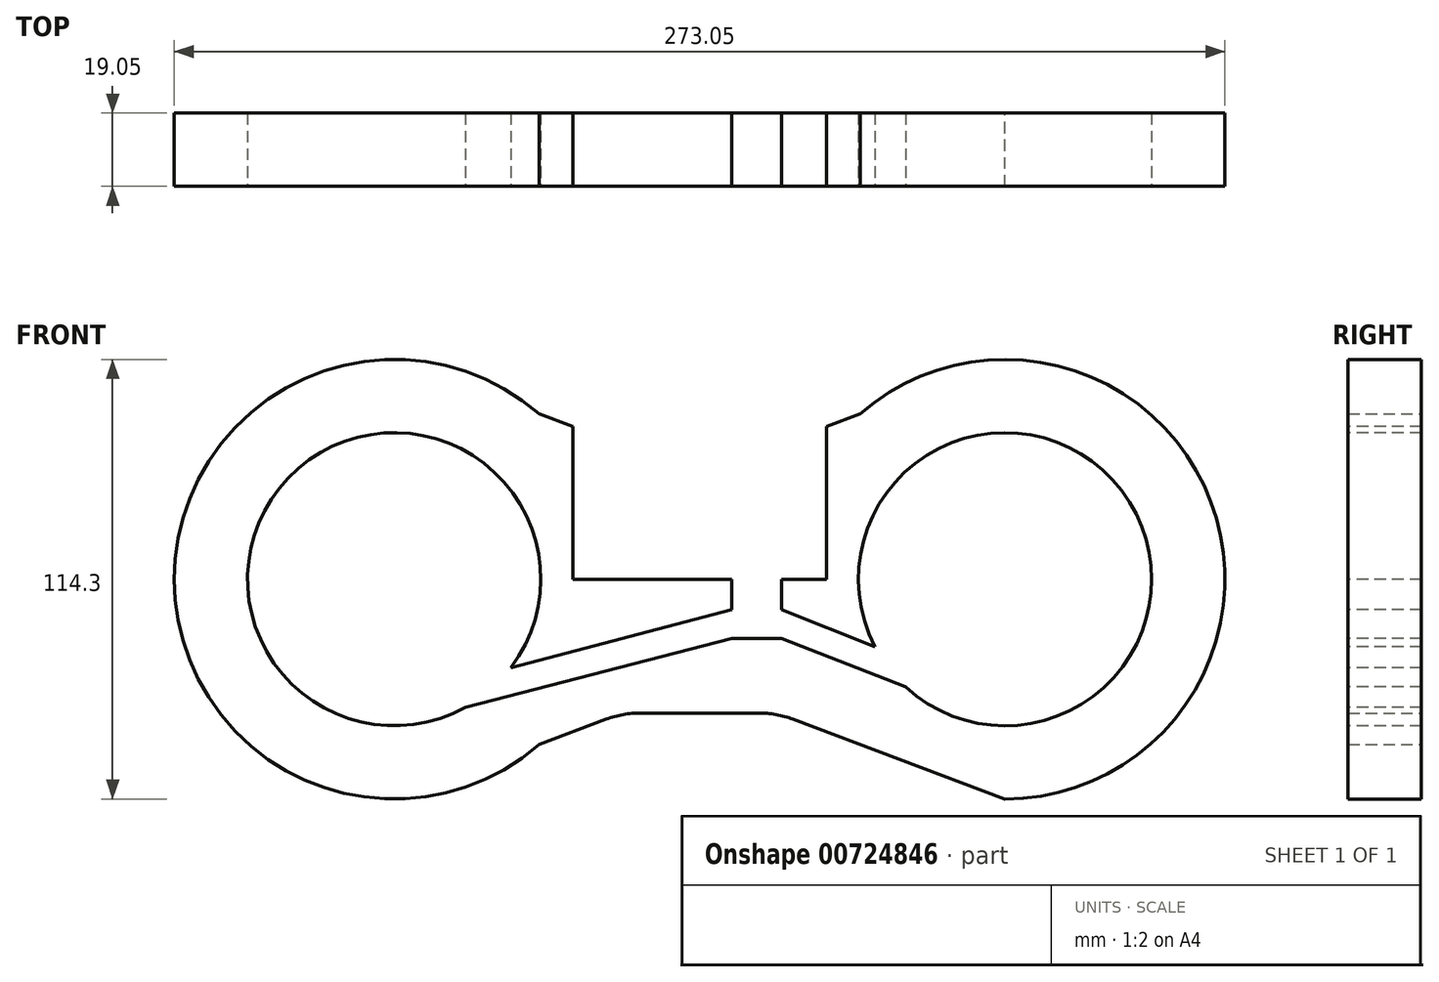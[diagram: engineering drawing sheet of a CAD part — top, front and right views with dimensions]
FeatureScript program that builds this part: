
annotation { "Feature Type Name" : "Feature", "Feature Type Description" : "" }
export const myFeature = defineFeature(function(context is Context, id is Id, definition is map)
    precondition{}
    {
        {
            var Q0;
            Q0=qCreatedBy(makeId("Front.planeOp"),FACE);
            var sketch = newSketch(context, id + "F0", { "sketchPlane" : qUnion([Q0])});
            skCircle(sketch, "E0", {"center": v(-35.08, 0) * mm, "radius": 57.15 * mm});
            skCircle(sketch, "E1", {"center": v(123.67, 0) * mm, "radius": 57.15 * mm});
            skLineSegment(sketch, "E2", {"start": v(-35.08, 57.15) * mm, "end": v(20.03, 36.4) * mm});
            skLineSegment(sketch, "E3", {"start": v(28.98, 34.78) * mm, "end": v(59.62, 34.78) * mm});
            skLineSegment(sketch, "E4", {"start": v(68.57, 36.4) * mm, "end": v(123.67, 57.15) * mm});
            skLineSegment(sketch, "E5", {"start": v(-35.08, -57.15) * mm, "end": v(20.03, -36.4) * mm});
            skLineSegment(sketch, "E6", {"start": v(28.98, -34.78) * mm, "end": v(59.62, -34.78) * mm});
            skLineSegment(sketch, "E7", {"start": v(68.57, -36.4) * mm, "end": v(123.67, -57.15) * mm});
            skPoint(sketch, "E8.visualSharp", {"position": v(24.35, 34.78) * mm});
            skArc(sketch, "E8.filletArc", {"start": v(20.03, 36.4) * mm, "mid": v(24.43, 35.19) * mm, "end": v(28.98, 34.78) * mm});
            skPoint(sketch, "E9.visualSharp", {"position": v(64.25, 34.78) * mm});
            skArc(sketch, "E9.filletArc", {"start": v(59.62, 34.78) * mm, "mid": v(64.17, 35.19) * mm, "end": v(68.57, 36.4) * mm});
            skPoint(sketch, "E10.visualSharp", {"position": v(24.35, -34.78) * mm});
            skArc(sketch, "E10.filletArc", {"start": v(28.98, -34.78) * mm, "mid": v(24.43, -35.19) * mm, "end": v(20.03, -36.4) * mm});
            skPoint(sketch, "E11.visualSharp", {"position": v(64.25, -34.78) * mm});
            skArc(sketch, "E11.filletArc", {"start": v(68.57, -36.4) * mm, "mid": v(64.17, -35.19) * mm, "end": v(59.62, -34.78) * mm});
            skSolve(sketch);
        }
        {
            var Q0;
            Q0=makeQuery(id+"F0.imprint","IMPRINT",FACE,{"disambiguationData":[TD([[makeQuery(id+"F0.imprint","IMPRINT",EDGE,{"derivedFrom":sQuery(id+"F0.wireOp",EDGE,"E3")}),-1.0]])]});
            var Q1;
            {var subQ0=sQuery(id+"F0.wireOp",EDGE,"E2");var subQ1=sQuery(id+"F0.wireOp",EDGE,"E0");var subQ2=makeQuery(id+"F0.imprint","INTERSECT",VERTEX,{"disambiguationData":[OD(0.0)],"derivedFrom":[subQ1,subQ0]});Q1=makeQuery(id+"F0.imprint","IMPRINT",FACE,{"disambiguationData":[TD([[makeQuery(id+"F0.imprint","IMPRINT",EDGE,{"disambiguationData":[TD([[subQ2,-1.0]])],"derivedFrom":subQ1}),1.0]])]});}
            var Q2;
            {var subQ0=sQuery(id+"F0.wireOp",EDGE,"E4");var subQ1=sQuery(id+"F0.wireOp",EDGE,"E1");var subQ2=makeQuery(id+"F0.imprint","INTERSECT",VERTEX,{"disambiguationData":[OD(1.0)],"derivedFrom":[subQ1,subQ0]});Q2=makeQuery(id+"F0.imprint","IMPRINT",FACE,{"disambiguationData":[TD([[makeQuery(id+"F0.imprint","IMPRINT",EDGE,{"disambiguationData":[TD([[subQ2,-1.0]])],"derivedFrom":subQ1}),1.0]])]});}
            var Q3;
            {var subQ0=sQuery(id+"F0.wireOp",EDGE,"E4");var subQ1=sQuery(id+"F0.wireOp",EDGE,"E1");var subQ2=makeQuery(id+"F0.imprint","INTERSECT",VERTEX,{"disambiguationData":[OD(0.0)],"derivedFrom":[subQ1,subQ0]});Q3=makeQuery(id+"F0.imprint","IMPRINT",FACE,{"disambiguationData":[TD([[makeQuery(id+"F0.imprint","IMPRINT",EDGE,{"disambiguationData":[TD([[subQ2,-1.0]])],"derivedFrom":subQ1}),1.0]])]});}
            var Q4;
            {var subQ0=sQuery(id+"F0.wireOp",EDGE,"E2");var subQ1=sQuery(id+"F0.wireOp",EDGE,"E0");var subQ2=makeQuery(id+"F0.imprint","INTERSECT",VERTEX,{"disambiguationData":[OD(0.0)],"derivedFrom":[subQ1,subQ0]});Q4=makeQuery(id+"F0.imprint","IMPRINT",FACE,{"disambiguationData":[TD([[makeQuery(id+"F0.imprint","IMPRINT",EDGE,{"disambiguationData":[TD([[subQ2,1.0]])],"derivedFrom":subQ1}),1.0]])]});}
            var Q5;
            {var subQ0=sQuery(id+"F0.wireOp",EDGE,"E5");var subQ1=sQuery(id+"F0.wireOp",EDGE,"E0");var subQ2=makeQuery(id+"F0.imprint","INTERSECT",VERTEX,{"disambiguationData":[OD(0.0)],"derivedFrom":[subQ1,subQ0]});Q5=makeQuery(id+"F0.imprint","IMPRINT",FACE,{"disambiguationData":[TD([[makeQuery(id+"F0.imprint","IMPRINT",EDGE,{"disambiguationData":[TD([[subQ2,-1.0]])],"derivedFrom":subQ1}),1.0]])]});}
            var Q6;
            {var subQ0=sQuery(id+"F0.wireOp",EDGE,"E7");var subQ1=sQuery(id+"F0.wireOp",EDGE,"E1");var subQ2=makeQuery(id+"F0.imprint","INTERSECT",VERTEX,{"disambiguationData":[OD(0.0)],"derivedFrom":[subQ1,subQ0]});Q6=makeQuery(id+"F0.imprint","IMPRINT",FACE,{"disambiguationData":[TD([[makeQuery(id+"F0.imprint","IMPRINT",EDGE,{"disambiguationData":[TD([[subQ2,1.0]])],"derivedFrom":subQ1}),1.0]])]});}
            extrude(context, id + "F1", {"entities" : qUnion([Q0, Q1, Q2, Q3, Q4, Q5, Q6]), "depth" : 19.05 * mm, "offsetDistance" : 25.4 * mm});
        }
        {
            var Q0;
            Q0=makeQuery(id+"F1.opExtrude","CAP_FACE",FACE,{"disambiguationData":[OSD([sQuery(id+"F0.wireOp",EDGE,"E0"),sQuery(id+"F0.wireOp",EDGE,"E1"),sQuery(id+"F0.wireOp",EDGE,"E2"),sQuery(id+"F0.wireOp",EDGE,"E3"),sQuery(id+"F0.wireOp",EDGE,"E4"),sQuery(id+"F0.wireOp",EDGE,"E5"),sQuery(id+"F0.wireOp",EDGE,"E6"),sQuery(id+"F0.wireOp",EDGE,"E7"),sQuery(id+"F0.wireOp",EDGE,"E8.filletArc"),sQuery(id+"F0.wireOp",EDGE,"E9.filletArc"),sQuery(id+"F0.wireOp",EDGE,"E10.filletArc"),sQuery(id+"F0.wireOp",EDGE,"E11.filletArc")])],"isStart":false});
            var sketch = newSketch(context, id + "F2", { "sketchPlane" : qUnion([Q0])});
            skCircle(sketch, "E12", {"center": v(-35.08, 0) * mm, "radius": 38.1 * mm});
            skCircle(sketch, "E13", {"center": v(123.67, 0) * mm, "radius": 38.1 * mm});
            skLineSegment(sketch, "E14", {"start": v(11.32, 39.69) * mm, "end": v(11.32, 0) * mm});
            skLineSegment(sketch, "E15", {"start": v(11.32, 0) * mm, "end": v(77.28, 0) * mm});
            skPoint(sketch, "E15.endSnap0", {"position": v(77.28, 39.69) * mm});
            skLineSegment(sketch, "E16", {"start": v(77.28, 0) * mm, "end": v(77.28, 39.69) * mm});
            skLineSegment(sketch, "E17", {"start": v(52.7, 0) * mm, "end": v(52.7, -7.87) * mm});
            skLineSegment(sketch, "E18", {"start": v(52.7, -7.87) * mm, "end": v(-35.08, -31.04) * mm});
            skLineSegment(sketch, "E19", {"start": v(-35.08, -31.04) * mm, "end": v(-35.08, -38.1) * mm});
            skLineSegment(sketch, "E20", {"start": v(-35.08, -38.1) * mm, "end": v(52.7, -15.4) * mm});
            skLineSegment(sketch, "E21", {"start": v(52.7, -15.4) * mm, "end": v(65.64, -15.4) * mm});
            skLineSegment(sketch, "E22", {"start": v(65.64, -15.4) * mm, "end": v(123.67, -38.1) * mm});
            skLineSegment(sketch, "E23", {"start": v(123.67, -38.1) * mm, "end": v(123.67, -31.04) * mm});
            skLineSegment(sketch, "E24", {"start": v(123.67, -31.04) * mm, "end": v(65.64, -7.87) * mm});
            skLineSegment(sketch, "E25", {"start": v(65.64, -7.87) * mm, "end": v(65.64, 0) * mm});
            skSolve(sketch);
        }
        {
            var Q0;
            {var subQ0=sQuery(id+"F2.wireOp",EDGE,"E19");Q0=makeQuery(id+"F2.imprint","IMPRINT",FACE,{"disambiguationData":[TD([[makeQuery(id+"F2.imprint","IMPRINT",EDGE,{"derivedFrom":subQ0}),-1.0]])]});}
            var Q1;
            {var subQ5=sQuery(id+"F2.wireOp",EDGE,"E19");Q1=makeQuery(id+"F2.imprint","IMPRINT",FACE,{"disambiguationData":[TD([[makeQuery(id+"F2.imprint","IMPRINT",EDGE,{"derivedFrom":subQ5}),1.0]])]});}
            var Q2;
            {var subQ0=sQuery(id+"F2.wireOp",EDGE,"E20");var subQ1=sQuery(id+"F2.wireOp",EDGE,"E12");var subQ3=makeQuery(id+"F2.imprint","INTERSECT",VERTEX,{"derivedFrom":[subQ1,subQ0]});Q2=makeQuery(id+"F2.imprint","IMPRINT",FACE,{"disambiguationData":[TD([[makeQuery(id+"F2.imprint","IMPRINT",EDGE,{"disambiguationData":[TD([[subQ3,1.0]])],"derivedFrom":subQ1}),1.0]])]});}
            var Q3;
            {var subQ0=sQuery(id+"F2.wireOp",EDGE,"E17");Q3=makeQuery(id+"F2.imprint","IMPRINT",FACE,{"disambiguationData":[TD([[makeQuery(id+"F2.imprint","IMPRINT",EDGE,{"derivedFrom":subQ0}),1.0]])]});}
            var Q4;
            {var subQ6=sQuery(id+"F2.wireOp",EDGE,"E14");Q4=makeQuery(id+"F2.imprint","IMPRINT",FACE,{"disambiguationData":[TD([[makeQuery(id+"F2.imprint","IMPRINT",EDGE,{"derivedFrom":subQ6}),1.0]])]});}
            var Q5;
            {var subQ0=sQuery(id+"F2.wireOp",EDGE,"E23");Q5=makeQuery(id+"F2.imprint","IMPRINT",FACE,{"disambiguationData":[TD([[makeQuery(id+"F2.imprint","IMPRINT",EDGE,{"derivedFrom":subQ0}),-1.0]])]});}
            var Q6;
            {var subQ0=sQuery(id+"F2.wireOp",EDGE,"E22");var subQ1=sQuery(id+"F2.wireOp",EDGE,"E13");var subQ3=makeQuery(id+"F2.imprint","INTERSECT",VERTEX,{"derivedFrom":[subQ1,subQ0]});Q6=makeQuery(id+"F2.imprint","IMPRINT",FACE,{"disambiguationData":[TD([[makeQuery(id+"F2.imprint","IMPRINT",EDGE,{"disambiguationData":[TD([[subQ3,-1.0]])],"derivedFrom":subQ1}),1.0]])]});}
            var Q7;
            {var subQ5=sQuery(id+"F2.wireOp",EDGE,"E23");Q7=makeQuery(id+"F2.imprint","IMPRINT",FACE,{"disambiguationData":[TD([[makeQuery(id+"F2.imprint","IMPRINT",EDGE,{"derivedFrom":subQ5}),1.0]])]});}
            extrude(context, id + "F3", {"entities" : qUnion([Q0, Q1, Q2, Q3, Q4, Q5, Q6, Q7]), "operationType" : NewBodyOperationType.REMOVE, "oppositeDirection" : true, "depth" : 25.4 * mm, "offsetDistance" : 25.4 * mm});
        }
    });
